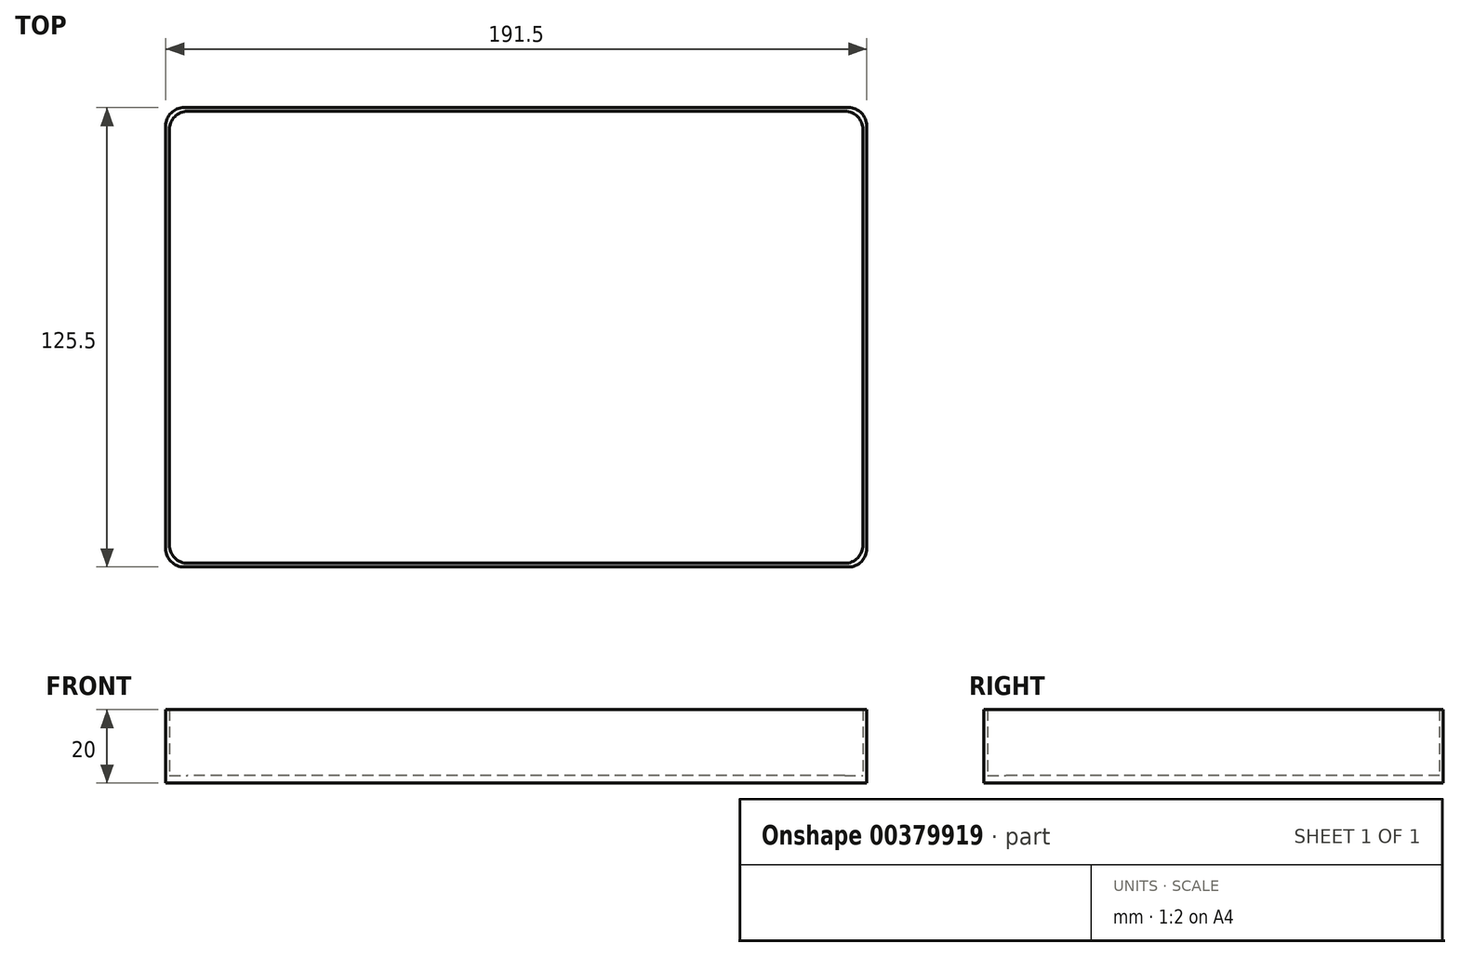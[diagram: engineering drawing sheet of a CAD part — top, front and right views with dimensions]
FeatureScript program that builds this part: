
annotation { "Feature Type Name" : "Feature", "Feature Type Description" : "" }
export const myFeature = defineFeature(function(context is Context, id is Id, definition is map)
    precondition{}
    {
        {
            var Q0;
            Q0=qCreatedBy(makeId("Top.planeOp"),FACE);
            var sketch = newSketch(context, id + "F0", { "sketchPlane" : qUnion([Q0])});
            skLineSegment(sketch, "E0.bottom", {"start": v(90.75, 62.75) * mm, "end": v(-90.75, 62.75) * mm});
            skLineSegment(sketch, "E0.top", {"start": v(90.75, -62.75) * mm, "end": v(-90.75, -62.75) * mm});
            skLineSegment(sketch, "E0.left", {"start": v(95.75, 57.75) * mm, "end": v(95.75, -57.75) * mm});
            skLineSegment(sketch, "E0.right", {"start": v(-95.75, 57.75) * mm, "end": v(-95.75, -57.75) * mm});
            skPoint(sketch, "E0.middle", {"position": v(0, 0) * mm});
            skLineSegment(sketch, "E1.bottom", {"start": v(89.75, 61.75) * mm, "end": v(-89.75, 61.75) * mm});
            skLineSegment(sketch, "E1.top", {"start": v(89.75, -61.75) * mm, "end": v(-89.75, -61.75) * mm});
            skLineSegment(sketch, "E1.left", {"start": v(94.75, 56.75) * mm, "end": v(94.75, -56.75) * mm});
            skLineSegment(sketch, "E1.right", {"start": v(-94.75, 56.75) * mm, "end": v(-94.75, -56.75) * mm});
            skPoint(sketch, "E2.visualSharp", {"position": v(-95.75, 62.75) * mm});
            skArc(sketch, "E2.filletArc", {"start": v(-90.75, 62.75) * mm, "mid": v(-94.29, 61.29) * mm, "end": v(-95.75, 57.75) * mm});
            skPoint(sketch, "E3.visualSharp", {"position": v(95.75, 62.75) * mm});
            skArc(sketch, "E3.filletArc", {"start": v(95.75, 57.75) * mm, "mid": v(94.29, 61.29) * mm, "end": v(90.75, 62.75) * mm});
            skPoint(sketch, "E4.visualSharp", {"position": v(95.75, -62.75) * mm});
            skArc(sketch, "E4.filletArc", {"start": v(90.75, -62.75) * mm, "mid": v(94.29, -61.29) * mm, "end": v(95.75, -57.75) * mm});
            skPoint(sketch, "E5.visualSharp", {"position": v(94.75, -61.75) * mm});
            skArc(sketch, "E5.filletArc", {"start": v(89.75, -61.75) * mm, "mid": v(93.29, -60.29) * mm, "end": v(94.75, -56.75) * mm});
            skPoint(sketch, "E6.visualSharp", {"position": v(94.75, 61.75) * mm});
            skArc(sketch, "E6.filletArc", {"start": v(94.75, 56.75) * mm, "mid": v(93.29, 60.29) * mm, "end": v(89.75, 61.75) * mm});
            skPoint(sketch, "E7.visualSharp", {"position": v(-95.75, -62.75) * mm});
            skArc(sketch, "E7.filletArc", {"start": v(-95.75, -57.75) * mm, "mid": v(-94.29, -61.29) * mm, "end": v(-90.75, -62.75) * mm});
            skPoint(sketch, "E8.visualSharp", {"position": v(-94.75, -61.75) * mm});
            skArc(sketch, "E8.filletArc", {"start": v(-94.75, -56.75) * mm, "mid": v(-93.29, -60.29) * mm, "end": v(-89.75, -61.75) * mm});
            skPoint(sketch, "E9.visualSharp", {"position": v(-94.75, 61.75) * mm});
            skArc(sketch, "E9.filletArc", {"start": v(-89.75, 61.75) * mm, "mid": v(-93.29, 60.29) * mm, "end": v(-94.75, 56.75) * mm});
            skSolve(sketch);
        }
        {
            var Q0;
            Q0=makeQuery(id+"F0.imprint","IMPRINT",FACE,{"disambiguationData":[TD([[makeQuery(id+"F0.imprint","IMPRINT",EDGE,{"derivedFrom":sQuery(id+"F0.wireOp",EDGE,"E0.bottom")}),1.0]])]});
            extrude(context, id + "F1", {"entities" : qUnion([Q0]), "depth" : 20 * mm});
        }
        {
            var Q0;
            Q0=qCreatedBy(makeId("Top.planeOp"),FACE);
            var sketch = newSketch(context, id + "F2", { "sketchPlane" : qUnion([Q0])});
            skLineSegment(sketch, "E10.bottom", {"start": v(90.75, 62.75) * mm, "end": v(-90.75, 62.75) * mm});
            skLineSegment(sketch, "E10.top", {"start": v(90.75, -62.75) * mm, "end": v(-90.75, -62.75) * mm});
            skLineSegment(sketch, "E10.left", {"start": v(95.75, 57.75) * mm, "end": v(95.75, -57.75) * mm});
            skLineSegment(sketch, "E10.right", {"start": v(-95.75, 57.75) * mm, "end": v(-95.75, -57.75) * mm});
            skPoint(sketch, "E10.middle", {"position": v(0, 0) * mm});
            skPoint(sketch, "E11.visualSharp", {"position": v(-95.75, 62.75) * mm});
            skArc(sketch, "E11.filletArc", {"start": v(-90.75, 62.75) * mm, "mid": v(-94.29, 61.29) * mm, "end": v(-95.75, 57.75) * mm});
            skPoint(sketch, "E12.visualSharp", {"position": v(-95.75, -62.75) * mm});
            skArc(sketch, "E12.filletArc", {"start": v(-95.75, -57.75) * mm, "mid": v(-94.29, -61.29) * mm, "end": v(-90.75, -62.75) * mm});
            skPoint(sketch, "E13.visualSharp", {"position": v(95.75, -62.75) * mm});
            skArc(sketch, "E13.filletArc", {"start": v(90.75, -62.75) * mm, "mid": v(94.29, -61.29) * mm, "end": v(95.75, -57.75) * mm});
            skPoint(sketch, "E14.visualSharp", {"position": v(95.75, 62.75) * mm});
            skArc(sketch, "E14.filletArc", {"start": v(95.75, 57.75) * mm, "mid": v(94.29, 61.29) * mm, "end": v(90.75, 62.75) * mm});
            skSolve(sketch);
        }
        {
            var Q0;
            Q0=makeQuery(id+"F2.imprint","IMPRINT",FACE,{"disambiguationData":[TD([[makeQuery(id+"F2.imprint","IMPRINT",EDGE,{"derivedFrom":sQuery(id+"F2.wireOp",EDGE,"E10.bottom")}),1.0]])]});
            extrude(context, id + "F3", {"entities" : qUnion([Q0]), "operationType" : NewBodyOperationType.ADD, "depth" : 2 * mm});
        }
    });
